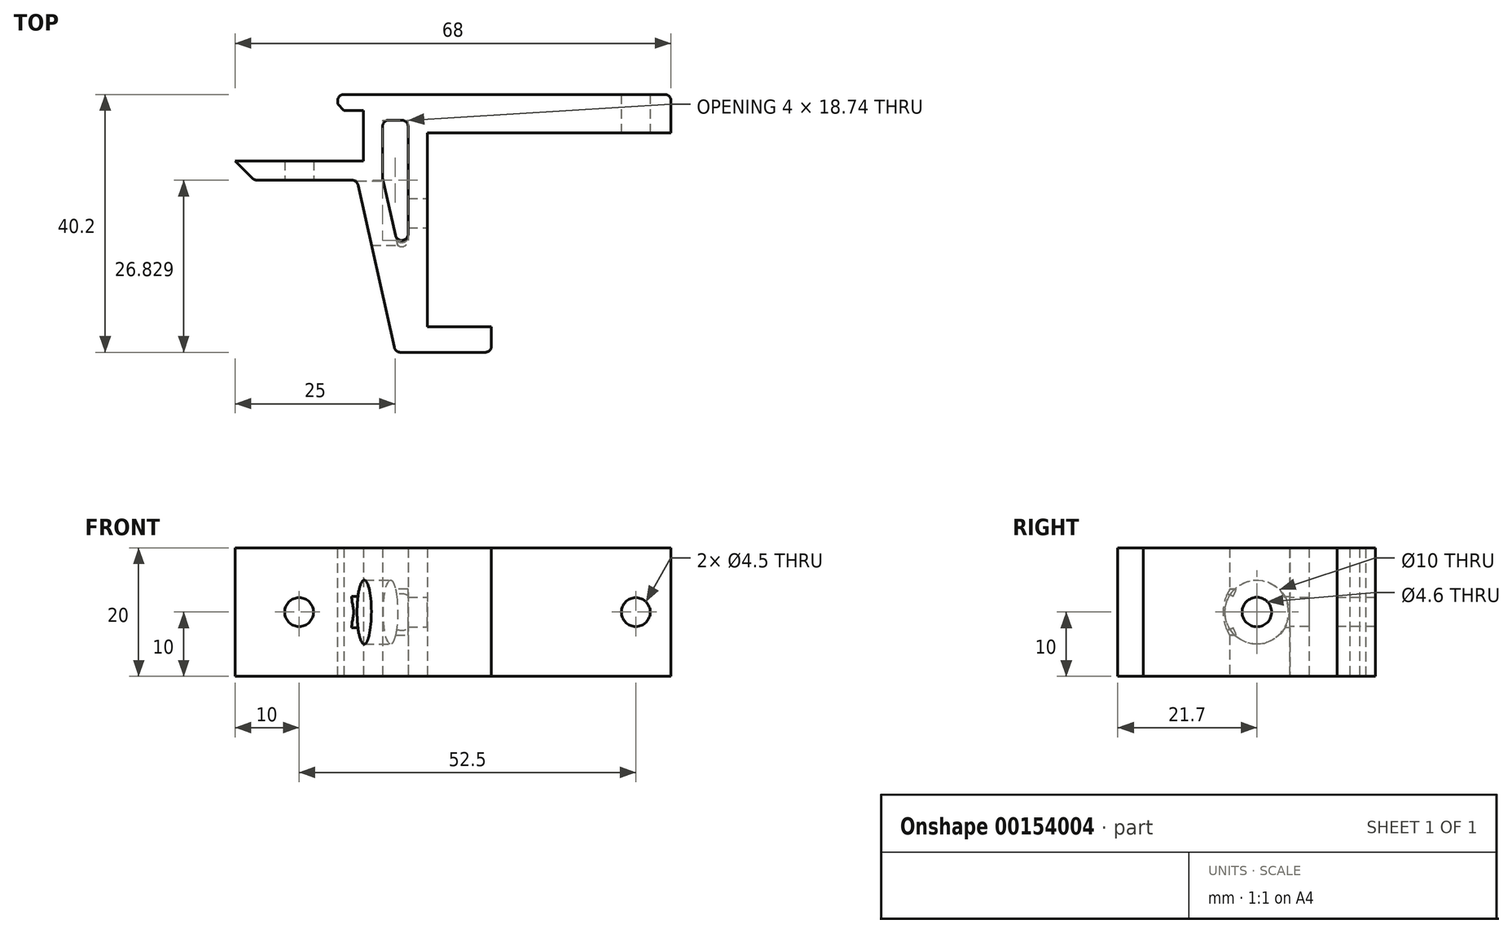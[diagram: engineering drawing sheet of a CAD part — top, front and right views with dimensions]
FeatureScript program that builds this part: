
annotation { "Feature Type Name" : "Feature", "Feature Type Description" : "" }
export const myFeature = defineFeature(function(context is Context, id is Id, definition is map)
    precondition{}
    {
        {
            var Q0;
            Q0=qCreatedBy(makeId("Top.planeOp"),FACE);
            var sketch = newSketch(context, id + "F0", { "sketchPlane" : qUnion([Q0])});
            skPoint(sketch, "E0.0", {"position": v(-10, -10) * mm});
            skPoint(sketch, "E1.0", {"position": v(10, -10) * mm});
            skLineSegment(sketch, "E2", {"start": v(-10, -10) * mm, "end": v(-10, -13) * mm});
            skLineSegment(sketch, "E3", {"start": v(-10, -13) * mm, "end": v(15, -13) * mm, "construction": true});
            skLineSegment(sketch, "E4", {"start": v(15, -13) * mm, "end": v(15, -39.85) * mm, "construction": true});
            skLineSegment(sketch, "E5", {"start": v(15, -39.85) * mm, "end": v(30, -39.85) * mm});
            skLineSegment(sketch, "E6", {"start": v(30, -39.85) * mm, "end": v(30, -35.85) * mm});
            skLineSegment(sketch, "E7", {"start": v(30, -35.85) * mm, "end": v(20, -35.85) * mm});
            skLineSegment(sketch, "E8", {"start": v(20, -35.85) * mm, "end": v(20, -5.65) * mm});
            skLineSegment(sketch, "E9", {"start": v(20, -5.65) * mm, "end": v(58, -5.65) * mm});
            skLineSegment(sketch, "E10", {"start": v(-10, -10) * mm, "end": v(10, -10) * mm});
            skLineSegment(sketch, "E11", {"start": v(10, -2.15) * mm, "end": v(8.5, -2.15) * mm});
            skLineSegment(sketch, "E12", {"start": v(6, -2.15) * mm, "end": v(6, 0.35) * mm});
            skLineSegment(sketch, "E13", {"start": v(6, 0.35) * mm, "end": v(58, 0.35) * mm});
            skLineSegment(sketch, "E14", {"start": v(58, 0.35) * mm, "end": v(58, -5.65) * mm});
            skLineSegment(sketch, "E15", {"start": v(15, -39.85) * mm, "end": v(9, -13) * mm});
            skLineSegment(sketch, "E16", {"start": v(-10, -13) * mm, "end": v(9, -13) * mm});
            skLineSegment(sketch, "E17", {"start": v(17, -3.65) * mm, "end": v(17, -30.46) * mm});
            skLineSegment(sketch, "E18", {"start": v(10, -2.15) * mm, "end": v(10, -10) * mm});
            skLineSegment(sketch, "E19", {"start": v(17, -3.65) * mm, "end": v(13, -3.65) * mm});
            skLineSegment(sketch, "E20", {"start": v(13, -3.65) * mm, "end": v(13, -12.56) * mm});
            skLineSegment(sketch, "E21", {"start": v(13, -12.56) * mm, "end": v(17, -30.46) * mm});
            skLineSegment(sketch, "E22", {"start": v(8.5, -2.15) * mm, "end": v(6, -2.15) * mm});
            skSolve(sketch);
        }
        {
            var Q0;
            Q0=makeQuery(id+"F0.imprint","IMPRINT",FACE,{"disambiguationData":[TD([[makeQuery(id+"F0.imprint","IMPRINT",EDGE,{"derivedFrom":sQuery(id+"F0.wireOp",EDGE,"E2")}),1.0]])]});
            extrude(context, id + "F1", {"entities" : qUnion([Q0]), "depth" : 20 * mm});
        }
        {
            var Q0;
            Q0=makeQuery(id+"F1.opExtrude","SWEPT_FACE",FACE,{"disambiguationData":[OSD([sQuery(id+"F0.wireOp",EDGE,"E9")])]});
            var sketch = newSketch(context, id + "F2", { "sketchPlane" : qUnion([Q0])});
            skLineSegment(sketch, "E23", {"start": v(20, 10) * mm, "end": v(58, 10) * mm, "construction": true});
            skCircle(sketch, "E24", {"center": v(52.5, 10) * mm, "radius": 2.25 * mm});
            skSolve(sketch);
        }
        {
            var Q0;
            Q0=makeQuery(id+"F1.opExtrude","SWEPT_FACE",FACE,{"disambiguationData":[OSD([sQuery(id+"F0.wireOp",EDGE,"E16")])]});
            var sketch = newSketch(context, id + "F3", { "sketchPlane" : qUnion([Q0])});
            skLineSegment(sketch, "E25", {"start": v(0, 20) * mm, "end": v(0, 0) * mm, "construction": true});
            skCircle(sketch, "E26", {"center": v(0, 10) * mm, "radius": 2.25 * mm});
            skSolve(sketch);
        }
        {
            var Q0;
            Q0=makeQuery(id+"F3.imprint","IMPRINT",FACE,{"disambiguationData":[TD([[makeQuery(id+"F3.imprint","IMPRINT",EDGE,{"derivedFrom":sQuery(id+"F3.wireOp",EDGE,"E26")}),1.0]])]});
            var Q1;
            Q1=makeQuery(id+"F2.imprint","IMPRINT",FACE,{"disambiguationData":[TD([[makeQuery(id+"F2.imprint","IMPRINT",EDGE,{"derivedFrom":sQuery(id+"F2.wireOp",EDGE,"E24")}),1.0]])]});
            extrude(context, id + "F4", {"entities" : qUnion([Q0, Q1]), "operationType" : NewBodyOperationType.REMOVE, "endBound" : BoundingType.UP_TO_NEXT, "oppositeDirection" : true, "depth" : 25 * mm});
        }
        {
            var Q0;
            Q0=makeQuery(id+"F1.opExtrude","SWEPT_FACE",FACE,{"disambiguationData":[OSD([sQuery(id+"F0.wireOp",EDGE,"E8")])]});
            var sketch = newSketch(context, id + "F5", { "sketchPlane" : qUnion([Q0])});
            skLineSegment(sketch, "E27", {"start": v(-18.15, 20) * mm, "end": v(-18.15, 0) * mm, "construction": true});
            skCircle(sketch, "E28", {"center": v(-18.15, 10) * mm, "radius": 2.3 * mm});
            skCircle(sketch, "E29", {"center": v(-18.15, 10) * mm, "radius": 5 * mm});
            skSolve(sketch);
        }
        {
            var Q0;
            Q0=makeQuery(id+"F5.imprint","IMPRINT",FACE,{"disambiguationData":[TD([[makeQuery(id+"F5.imprint","IMPRINT",EDGE,{"derivedFrom":sQuery(id+"F5.wireOp",EDGE,"E28")}),-1.0]])]});
            var Q1;
            Q1=makeQuery(id+"F1.opExtrude","SWEPT_FACE",FACE,{"disambiguationData":[OSD([sQuery(id+"F0.wireOp",EDGE,"E15")])]});
            var Q2;
            Q2=makeQuery(id+"F1.opExtrude","SWEPT_FACE",FACE,{"disambiguationData":[OSD([sQuery(id+"F0.wireOp",EDGE,"E17")])]});
            extrude(context, id + "F6", {"entities" : qUnion([Q0]), "operationType" : NewBodyOperationType.REMOVE, "endBound" : BoundingType.UP_TO_SURFACE, "oppositeDirection" : true, "endBoundEntityFace" : qUnion([Q1]), "depth" : 25 * mm, "hasSecondDirection" : true, "secondDirectionBound" : SecondDirectionBoundingType.UP_TO_SURFACE, "secondDirectionOppositeDirection" : true, "secondDirectionBoundEntityFace" : qUnion([Q2]), "secondDirectionDepth" : 25 * mm});
        }
        {
            var Q0;
            Q0=makeQuery(id+"F5.imprint","IMPRINT",FACE,{"disambiguationData":[TD([[makeQuery(id+"F5.imprint","IMPRINT",EDGE,{"derivedFrom":sQuery(id+"F5.wireOp",EDGE,"E28")}),1.0]])]});
            extrude(context, id + "F7", {"entities" : qUnion([Q0]), "operationType" : NewBodyOperationType.REMOVE, "endBound" : BoundingType.THROUGH_ALL, "oppositeDirection" : true, "depth" : 25 * mm});
        }
        {
            var Q0;
            Q0=makeQuery(id+"F1.opExtrude","SWEPT_EDGE",EDGE,{"disambiguationData":[OSD([sQuery(id+"F0.wireOp",EDGE,"E2"),sQuery(id+"F0.wireOp",EDGE,"E16")])]});
            chamfer(context, id + "F8", {"entities" : qUnion([Q0]), "width" : 3 * mm, "tangentPropagation" : true});
        }
        {
            var Q0;
            Q0=makeQuery(id+"F1.opExtrude","SWEPT_EDGE",EDGE,{"disambiguationData":[OSD([sQuery(id+"F0.wireOp",EDGE,"E5"),sQuery(id+"F0.wireOp",EDGE,"E15")])]});
            var Q1;
            Q1=makeQuery(id+"F1.opExtrude","SWEPT_EDGE",EDGE,{"disambiguationData":[OSD([sQuery(id+"F0.wireOp",EDGE,"E5"),sQuery(id+"F0.wireOp",EDGE,"E6")])]});
            var Q2;
            Q2=makeQuery(id+"F1.opExtrude","SWEPT_EDGE",EDGE,{"disambiguationData":[OSD([sQuery(id+"F0.wireOp",EDGE,"E19"),sQuery(id+"F0.wireOp",EDGE,"E20")])]});
            var Q3;
            Q3=makeQuery(id+"F1.opExtrude","SWEPT_EDGE",EDGE,{"disambiguationData":[OSD([sQuery(id+"F0.wireOp",EDGE,"E17"),sQuery(id+"F0.wireOp",EDGE,"E19")])]});
            var Q4;
            Q4=makeQuery(id+"F1.opExtrude","SWEPT_EDGE",EDGE,{"disambiguationData":[OSD([sQuery(id+"F0.wireOp",EDGE,"E20"),sQuery(id+"F0.wireOp",EDGE,"E21")])]});
            var Q5;
            Q5=makeQuery(id+"F1.opExtrude","SWEPT_EDGE",EDGE,{"disambiguationData":[OSD([sQuery(id+"F0.wireOp",EDGE,"E17"),sQuery(id+"F0.wireOp",EDGE,"E21")])]});
            var Q6;
            Q6=makeQuery(id+"F1.opExtrude","SWEPT_EDGE",EDGE,{"disambiguationData":[OSD([sQuery(id+"F0.wireOp",EDGE,"E12"),sQuery(id+"F0.wireOp",EDGE,"E13")])]});
            var Q7;
            Q7=makeQuery(id+"F1.opExtrude","SWEPT_EDGE",EDGE,{"disambiguationData":[OSD([sQuery(id+"F0.wireOp",EDGE,"E13"),sQuery(id+"F0.wireOp",EDGE,"E14")])]});
            var Q8;
            Q8=makeQuery(id+"F1.opExtrude","SWEPT_EDGE",EDGE,{"disambiguationData":[OSD([sQuery(id+"F0.wireOp",EDGE,"E15"),sQuery(id+"F0.wireOp",EDGE,"E16")])]});
            var Q9;
            {var subQ0=sQuery(id+"F0.wireOp",EDGE,"E16");Q9=makeQuery(id+"F8.opChamfer","BLEND_EDGE",EDGE,{"blendedFrom":[makeQuery(id+"F1.opExtrude","SWEPT_EDGE",EDGE,{"disambiguationData":[OSD([sQuery(id+"F0.wireOp",EDGE,"E2"),subQ0])]}),makeQuery(id+"F1.opExtrude","SWEPT_FACE",FACE,{"disambiguationData":[OSD([subQ0])]})],"blendedInto":[makeQuery(id+"F1.opExtrude","SWEPT_FACE",FACE,{"disambiguationData":[OSD([subQ0])]})]});}
            fillet(context, id + "F9", {"entities" : qUnion([Q0, Q1, Q2, Q3, Q4, Q5, Q6, Q7, Q8, Q9]), "radius" : 1 * mm, "tangentPropagation" : true, "allowEdgeOverflow" : false});
        }
        {
            var Q0;
            Q0=makeQuery(id+"F1.opExtrude","SWEPT_EDGE",EDGE,{"disambiguationData":[OSD([sQuery(id+"F0.wireOp",EDGE,"E12"),sQuery(id+"F0.wireOp",EDGE,"E22")])]});
            chamfer(context, id + "F10", {"entities" : qUnion([Q0]), "width" : 1 * mm, "tangentPropagation" : true});
        }
    });
